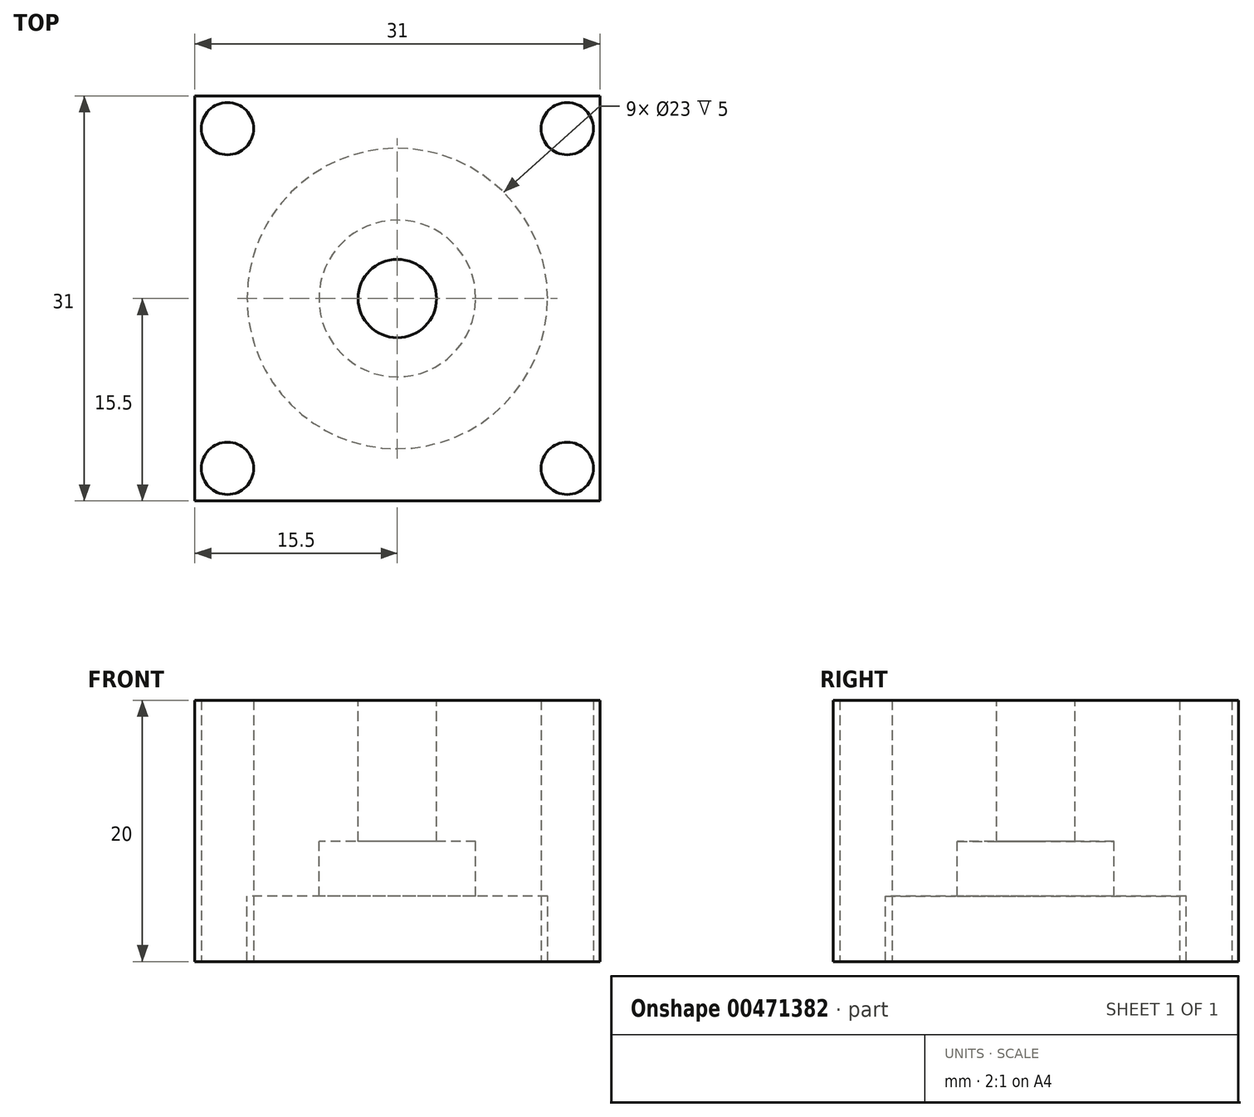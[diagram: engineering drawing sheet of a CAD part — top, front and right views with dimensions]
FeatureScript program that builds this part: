
annotation { "Feature Type Name" : "Feature", "Feature Type Description" : "" }
export const myFeature = defineFeature(function(context is Context, id is Id, definition is map)
    precondition{}
    {
        {
            var Q0;
            Q0=qCreatedBy(makeId("Top.planeOp"),FACE);
            var sketch = newSketch(context, id + "F0", { "sketchPlane" : qUnion([Q0])});
            skLineSegment(sketch, "E0.bottom", {"start": v(15.5, 15.5) * mm, "end": v(-15.5, 15.5) * mm});
            skLineSegment(sketch, "E0.top", {"start": v(15.5, -15.5) * mm, "end": v(-15.5, -15.5) * mm});
            skLineSegment(sketch, "E0.left", {"start": v(15.5, 15.5) * mm, "end": v(15.5, -15.5) * mm});
            skLineSegment(sketch, "E0.right", {"start": v(-15.5, 15.5) * mm, "end": v(-15.5, -15.5) * mm});
            skPoint(sketch, "E0.middle", {"position": v(0, 0) * mm});
            skCircle(sketch, "E1", {"center": v(-13, 13) * mm, "radius": 2 * mm});
            skCircle(sketch, "E2.MirrorC", {"center": v(13, 13) * mm, "radius": 2 * mm});
            skCircle(sketch, "E3.MirrorC", {"center": v(13, -13) * mm, "radius": 2 * mm});
            skCircle(sketch, "E4.MirrorC", {"center": v(-13, -13) * mm, "radius": 2 * mm});
            skSolve(sketch);
        }
        {
            var Q0;
            Q0=makeQuery(id+"F0.imprint","IMPRINT",FACE,{"disambiguationData":[TD([[makeQuery(id+"F0.imprint","IMPRINT",EDGE,{"derivedFrom":sQuery(id+"F0.wireOp",EDGE,"E0.bottom")}),1.0]])]});
            extrude(context, id + "F1", {"entities" : qUnion([Q0]), "depth" : 20 * mm});
        }
        {
            var Q0;
            Q0=qCreatedBy(makeId("Front.planeOp"),FACE);
            var sketch = newSketch(context, id + "F2", { "sketchPlane" : qUnion([Q0])});
            skLineSegment(sketch, "E5", {"start": v(0, 0) * mm, "end": v(0, 20) * mm});
            skLineSegment(sketch, "E6", {"start": v(0, 0) * mm, "end": v(11.5, 0) * mm});
            skLineSegment(sketch, "E7", {"start": v(11.5, 0) * mm, "end": v(11.5, 5) * mm});
            skLineSegment(sketch, "E8", {"start": v(11.5, 5) * mm, "end": v(6, 5) * mm});
            skLineSegment(sketch, "E9", {"start": v(6, 5) * mm, "end": v(6, 9.2) * mm});
            skLineSegment(sketch, "E10", {"start": v(6, 9.2) * mm, "end": v(3, 9.2) * mm});
            skLineSegment(sketch, "E11", {"start": v(0, 20) * mm, "end": v(3, 20) * mm});
            skLineSegment(sketch, "E12", {"start": v(3, 20) * mm, "end": v(3, 9.2) * mm});
            skLineSegment(sketch, "E13", {"start": v(0, 0) * mm, "end": v(0, 24.83) * mm, "construction": true});
            skSolve(sketch);
        }
        {
            var Q0;
            Q0 = qSketchRegion(id + "F2", true);
            var Q1;
            Q1=sQuery(id+"F2.wireOp",EDGE,"E13");
            revolve(context, id + "F3", {"operationType" : NewBodyOperationType.REMOVE, "entities" : qUnion([Q0]), "axis" : qUnion([Q1]), "revolveType" : RevolveType.FULL, "oppositeDirection" : true});
        }
    });
